# Revit family: Вентиляторы LITENED VRS
name_source: partatom
category: Оборудование
revit_build: Autodesk Revit 2017 (Build: 20160225_1515(x64)
units: mm (PartAtom-declared; Revit-internal decimal feet)

## family parameters
Всегда вертикально = Да
На основе рабочей плоскости = Нет
Общий = Нет
При загрузке вырезать с полостями = Нет
Размер круглого соединителя = Использовать диаметр
Тип детали = Нормальный
Точка расчета площади = Нет

## types (32) — shared parameters
h = 60 мм
Единица измерения = шт.
Завод изготовитель = NED
Ключевая пометка = Вентиляция
Наименование и тех.хар-ка = Радиальный вентилятор шумоизолированный с вперед загнутыми лопатками
Раздел = ОВ
высота ножек = 50 мм

## per-type parameters (varying)
| type | А | А1 | Б | Б1 | Г | Д | Д1 | Масса единицы | Материал | Мощность двигателя N,Вт | Напряжение U,В | Сила тока J, А | Тип, марка, обозначение | Частота вращения n, об/мин | высота | размер В | ширина |
| 50-25 VRS.22.4E | 710 мм | 690 мм | 470 мм | 450 мм | 395 мм | 615 мм | 595 мм | 46 | Сталь серая | 480 | 1х220 | 2,3 | LITENED 50-25 VRS. 22.4E | 1418 | 250 мм | 635 мм | 500 мм |
| 50-25 VRS.22.4D | 710 мм | 690 мм | 470 мм | 450 мм | 395 мм | 615 мм | 595 мм | 45,5 | RAL 0000 Серый металл | 520 | 3х380/1x220 | 0,95/1,65 | LITENED 50-25 VRS.22.4D | 1428 | 250 мм | 635 мм | 500 мм |
| 50-25 VRS.22.6D | 710 мм | 690 мм | 470 мм | 450 мм | 395 мм | 615 мм | 595 мм | 44,5 | Сталь серая | 230 | 3х380/1x220 | 0,46/0,8 | LITENED 50-25 VRS.22.6D | 952 | 250 мм | 635 мм | 500 мм |
| 50-25 VRS.25.4E (M) | 710 мм | 690 мм | 470 мм | 450 мм | 395 мм | 650 мм | 630 мм | 50,5 | Сталь серая | 820 | 1x220 | 3,7 | LITENED 50-25 VRS.25.4E (M) | 1390 | 250 мм | 635 мм | 500 мм |
| 50-25 VRS.25.4D (M) | 710 мм | 690 мм | 470 мм | 450 мм | 395 мм | 650 мм | 630 мм | 50 | Сталь серая | 940 | 3х380/1x220 | 2,2/3,8 | LITENED 50-25 VRS.25.4D (M) | 1461 | 250 мм | 635 мм | 500 мм |
| 50-25 VRS.25.6D (M) | 710 мм | 690 мм | 470 мм | 450 мм | 395 мм | 650 мм | 630 мм | 47 | Сталь серая | 360 | 3х380/1x220 | 0,92/1,6 | LITENED 50-25 VRS.25.6D (M) | 930 | 250 мм | 635 мм | 500 мм |
| 50-30 VRS.25.4E | 710 мм | 690 мм | 520 мм | 500 мм | 445 мм | 650 мм | 630 мм | 52 | Сталь серая | 820 | 1x220 | 3,7 | LITENED 50-30 VRS.25.4E | 1390 | 300 мм | 635 мм | 500 мм |
| 50-30 VRS.25.4D | 710 мм | 690 мм | 520 мм | 500 мм | 445 мм | 650 мм | 630 мм | 51,5 | Сталь серая | 940 | 3x380/1x220 | 2,2/3,8 | LITENED 50-30 VRS.25.4D | 1461 | 300 мм | 635 мм | 500 мм |
| 50-30 VRS.25.6D | 710 мм | 690 мм | 520 мм | 500 мм | 445 мм | 650 мм | 630 мм | 48,5 | Сталь серая | 360 | 3x380/1x220 | 0,92/1,6 | LITENED 50-30 VRS.25.6D | 930 | 300 мм | 635 мм | 500 мм |
| 50-30 VRS.28.4E (M) | 710 мм | 690 мм | 520 мм | 500 мм | 445 мм | 730 мм | 710 мм | 61 | Сталь серая | 1150 | 1x220 | 5,1 | LITENED 50-30 VRS.28.4E (M) | 1370 | 300 мм | 635 мм | 500 мм |
| 50-30 VRS.28.4D (M) | 710 мм | 690 мм | 520 мм | 500 мм | 445 мм | 730 мм | 710 мм | 60 | Сталь серая | 1740 | 3x380/1x220 | 2,6/4,5 | LITENED 50-30 VRS.28.4D (M) | 1415 | 300 мм | 635 мм | 500 мм |
| 50-30 VRS.28.6D (M) | 710 мм | 690 мм | 520 мм | 500 мм | 445 мм | 730 мм | 710 мм | 52 | Сталь серая | 580 | 3x380/1x220 | 1,3/2,25 | LITENED 50-30 VRS.28.6D (M) | 955 | 300 мм | 635 мм | 500 мм |
| 60-30 VRS.28.4E | 810 мм | 790 мм | 520 мм | 500 мм | 445 мм | 730 мм | 710 мм | 63,5 | Сталь серая | 1150 | 1x220 | 5,1 | LITENED 60-30 VRS.28.4E | 1370 | 300 мм | 735 мм | 600 мм |
| 60-30 VRS.28.4D | 810 мм | 790 мм | 520 мм | 500 мм | 445 мм | 730 мм | 710 мм | 63 | Сталь серая | 1740 | 3x380/1x220 | 2,6/4,5 | LITENED 60-30 VRS.28.4D | 1415 | 300 мм | 735 мм | 600 мм |
| 60-30 VRS.28.6D | 810 мм | 790 мм | 520 мм | 500 мм | 445 мм | 730 мм | 710 мм | 55,2 | Сталь серая | 580 | 3x380/1x220 | 1,3/2,25 | LITENED 60-30 VRS.28.6D | 955 | 300 мм | 735 мм | 600 мм |
| 60-30 VRS.31.4D (M) | 810 мм | 790 мм | 520 мм | 500 мм | 445 мм | 840 мм | 820 мм | 74 | Сталь серая | 2480 | 3x380/1x220 | 4,9/8,5 | LITENED 60-30 VRS.31.4D (M) | 1415 | 300 мм | 735 мм | 600 мм |
| 60-30 VRS.31.6D (M) | 810 мм | 790 мм | 520 мм | 500 мм | 445 мм | 840 мм | 820 мм | 68 | Сталь серая | 1850 | 3x380/1x220 | 1,8/3,1 | LITENED 60-30 VRS.31.6D (M) | 930 | 300 мм | 735 мм | 600 мм |
| 60-35 VRS.31.4D | 810 мм | 790 мм | 570 мм | 550 мм | 495 мм | 840 мм | 820 мм | 75 | Сталь серая | 2480 | 3x380/1x220 | 4,9/8,5 | LITENED 60-35 VRS.31.4D | 1415 | 350 мм | 735 мм | 600 мм |
| 60-35 VRS.31.6D | 810 мм | 790 мм | 570 мм | 550 мм | 495 мм | 840 мм | 820 мм | 69 | Сталь серая | 1850 | 3x380/1x220 | 1,8/3,1 | LITENED 60-35 VRS.31.6D | 930 | 350 мм | 735 мм | 600 мм |
| 60-35 VRS.35.4D (M) | 810 мм | 790 мм | 570 мм | 550 мм | 495 мм | 865 мм | 845 мм | 91,5 | Сталь серая | 3350 | 3x380/1x220 | 6,0/10,5 | LITENED 60-35 VRS.35.4D (M) | 1422 | 350 мм | 735 мм | 600 мм |
| 60-35 VRS.35.6D (M) | 810 мм | 790 мм | 570 мм | 550 мм | 495 мм | 865 мм | 845 мм | 77 | Сталь серая | 1100 | 3x380/1x220 | 2,0/3,5 | LITENED 60-35 VRS.35.6D (M) | 925 | 350 мм | 735 мм | 600 мм |
| 70-40 VRS.35.4D | 910 мм | 890 мм | 620 мм | 600 мм | 545 мм | 865 мм | 845 мм | 97 | Сталь серая | 3350 | 3x380/1x220 | 6,0/10,5 | LITENED 70-40 VRS.35.4D | 1422 | 400 мм | 835 мм | 700 мм |
| 70-40 VRS.35.6D | 910 мм | 890 мм | 620 мм | 600 мм | 545 мм | 865 мм | 845 мм | 83 | Сталь серая | 1100 | 3x380/1x220 | 2,0/3,5 | LITENED 70-40 VRS.35.6D | 925 | 400 мм | 835 мм | 700 мм |
| 70-40 VRS.35.8D | 910 мм | 890 мм | 620 мм | 600 мм | 545 мм | 865 мм | 845 мм | 83 | Сталь серая | 650 | 3x380/1x220 | 1,4/2,3 | LITENED 70-40 VRS.35.8D | 670 | 400 мм | 835 мм | 700 мм |
| 80-50 VRS.40.4D | 1010 мм | 990 мм | 720 мм | 700 мм | 645 мм | 975 мм | 955 мм | 122 | Сталь серая | 4980 | 3x380 | 8,1 | LITENED 80-50 VRS.40.4D | 1415 | 500 мм | 935 мм | 800 мм |
| 80-50 VRS.40.6D | 1010 мм | 990 мм | 720 мм | 700 мм | 645 мм | 975 мм | 955 мм | 115 | Сталь серая | 2810 | 3x380/1x220 | 5,1/8,8 | LITENED 80-50 VRS.40.6D | 945 | 500 мм | 935 мм | 800 мм |
| 80-50 VRS.40.8D | 1010 мм | 990 мм | 720 мм | 700 мм | 645 мм | 975 мм | 955 мм | 101 | Сталь серая | 1240 | 3x380/1x220 | 2,29/4,0 | LITENED 80-50 VRS.40.8D | 701 | 500 мм | 935 мм | 800 мм |
| 80-50 VRS.45.4D (M) | 1010 мм | 990 мм | 720 мм | 700 мм | 645 мм | 1100 мм | 1080 мм | 132 | Сталь серая | 4900 | 3x380 | 8,3 | LITENED 80-50 VRS.45.4D (M) | 1265 | 500 мм | 935 мм | 800 мм |
| 80-50 VRS.45.6D (M) | 1010 мм | 990 мм | 720 мм | 700 мм | 645 мм | 1100 мм | 1080 мм | 132 | Сталь серая | 3750 | 3x380/1x220 | 6,8/11,8 | LITENED 80-50 VRS.45.6D (M) | 930 | 500 мм | 935 мм | 800 мм |
| 90-50 VRS.45.4D | 1125 мм | 1105 мм | 740 мм | 720 мм | 645 мм | 1100 мм | 1080 мм | 142 | Сталь серая | 4900 | 3x380 | 8,3 | LITENED 90-50 VRS.45.4D | 1265 | 500 мм | 1050 мм | 900 мм |
| 90-50 VRS.45.6D | 1125 мм | 1105 мм | 740 мм | 720 мм | 645 мм | 1100 мм | 1080 мм | 142 | Сталь серая | 3750 | 3x380/1x220 | 6,8/11,8 | LITENED 90-50 VRS.45.6D | 930 | 500 мм | 1050 мм | 900 мм |
| 90-50 VRS.45.8D | 1125 мм | 1105 мм | 740 мм | 720 мм | 645 мм | 1100 мм | 1080 мм | 136 | Сталь серая | 1850 | 3x380/1x220 | 3,8/6,6 | LITENED 90-50 VRS.45.8D | 690 | 500 мм | 1050 мм | 900 мм |
